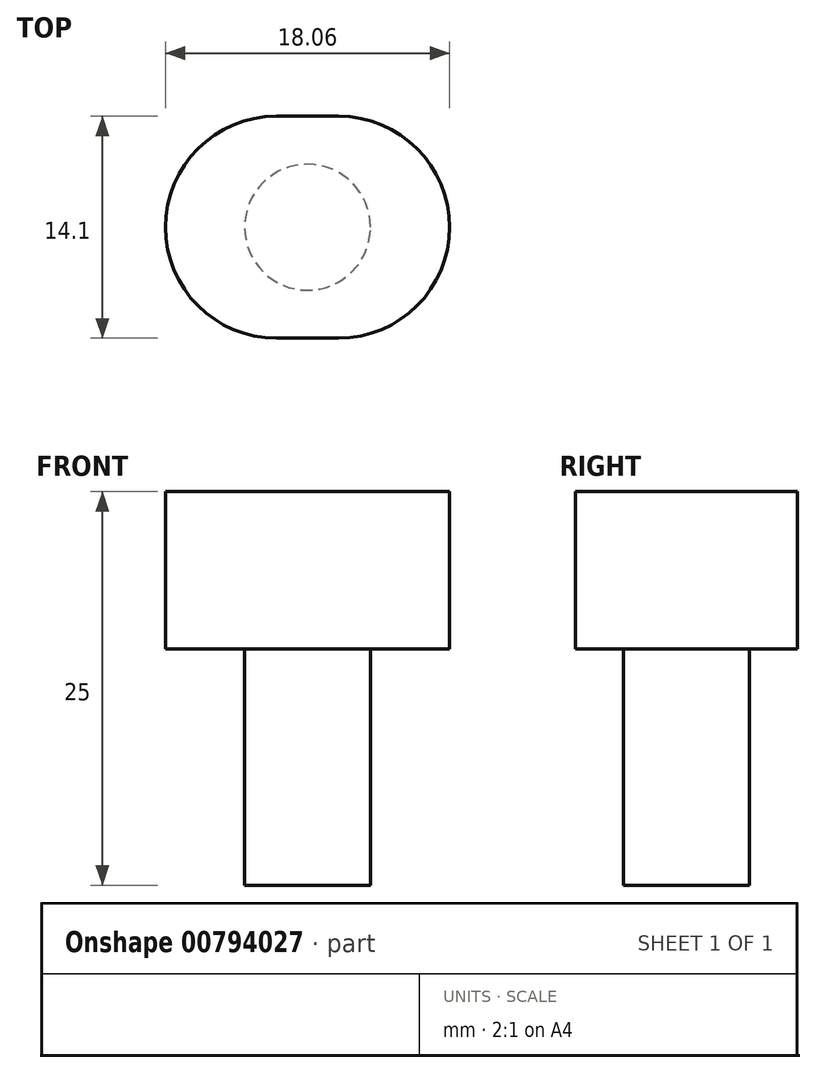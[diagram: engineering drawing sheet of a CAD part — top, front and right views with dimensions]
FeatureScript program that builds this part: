
annotation { "Feature Type Name" : "Feature", "Feature Type Description" : "" }
export const myFeature = defineFeature(function(context is Context, id is Id, definition is map)
    precondition{}
    {
        {
            var Q0;
            Q0=qCreatedBy(makeId("Top.planeOp"),FACE);
            var sketch = newSketch(context, id + "F0", { "sketchPlane" : qUnion([Q0])});
            skCircle(sketch, "E0", {"center": v(0, 0) * mm, "radius": 4 * mm});
            skSolve(sketch);
        }
        {
            var Q0;
            Q0=qSketchRegion(id+"F0",true);
            extrude(context, id + "F1", {"entities" : qUnion([Q0]), "depth" : 15 * mm, "offsetDistance" : 25.4 * mm});
        }
        {
            var Q0;
            Q0=makeQuery(id+"F1.opExtrude","CAP_FACE",FACE,{"disambiguationData":[OSD([sQuery(id+"F0.wireOp",EDGE,"E0")])],"isStart":false});
            var sketch = newSketch(context, id + "F2", { "sketchPlane" : qUnion([Q0])});
            skLineSegment(sketch, "E1", {"start": v(0, 0) * mm, "end": v(8, 0) * mm});
            skLineSegment(sketch, "E2", {"start": v(0, 0) * mm, "end": v(-8, 0) * mm});
            skLineSegment(sketch, "E3", {"start": v(0, 0) * mm, "end": v(0, 7.05) * mm});
            skLineSegment(sketch, "E4", {"start": v(0, 0) * mm, "end": v(0, -7.05) * mm});
            skLineSegment(sketch, "E5", {"start": v(8, 0) * mm, "end": v(1.97, 0) * mm});
            skLineSegment(sketch, "E6", {"start": v(-8, 0) * mm, "end": v(-1.98, 0) * mm});
            skArc(sketch, "E7", {"start": v(1.97, -7.05) * mm, "mid": v(9.03, 0) * mm, "end": v(1.97, 7.05) * mm});
            skArc(sketch, "E8", {"start": v(-1.98, -7.05) * mm, "mid": v(-9.03, 0) * mm, "end": v(-1.98, 7.05) * mm});
            skLineSegment(sketch, "E9", {"start": v(-1.98, 7.05) * mm, "end": v(1.97, 7.05) * mm});
            skLineSegment(sketch, "E10", {"start": v(1.97, -7.05) * mm, "end": v(-1.98, -7.05) * mm});
            skSolve(sketch);
        }
        {
            var Q0;
            Q0=qSketchRegion(id+"F2",true);
            extrude(context, id + "F3", {"entities" : qUnion([Q0]), "operationType" : NewBodyOperationType.ADD, "depth" : 10 * mm, "offsetDistance" : 25 * mm});
        }
    });
